# Revit family: Construction_Roof-Accessories_Alpine-SnowGuards_PD41
name_source: partatom
category: Specialty Equipment
units: mm (PartAtom-declared; Revit-internal decimal feet)

## family parameters
Cut with Voids When Loaded = No
Host = Face
OmniClass Number = 23.35.20.31.27.14
OmniClass Title = Snow Guards
Part Type = Normal
Room Calculation Point = No
Round Connector Dimension = Use Diameter
Shared = No

## types (5) — shared parameters
Assembly Code = B3010
Default Elevation = 48"
Description = PD41 Half Round Pad Style Snow Guard With Hook
Edition number = 1
Keynote = 07720
Manufacturer = Alpine SnowGuards
Model = PD 41
PD 410F = No
Product Guid = ab2724ba-9bd9-445f-86f5-17aeb9849d5a
Product Material = Alpine SnowGuards - Copper - Mill Finish
Product data url = https://www.bimobject.com
URL = https://www.alpinesnowguards.com
z_Option1 = Row Options : One Row
z_Option2 = Row Options : Two Rows
z_Option3 = Row Options : Three Rows

## per-type parameters (varying)
| type | Horizontal Spacing | Number of Rows | Vertical Spacing | Z_CR | Z_Horizontal Spacing | Z_Vertical Spacing |
| 3-Row Pattern | 24" | Row Options : Three Rows | 12" | No | 24" | 12" |
| 2x4 Pattern – Two Row | 48" | Row Options : Two Rows | 24" | No | 48" | 24" |
| 2x3 Pattern – Two Row | 36" | Row Options : Two Rows | 24" | No | 36" | 24" |
| 2x2 Pattern – Two Row | 24" | Row Options : Two Rows | 24" | No | 24" | 24" |
| Custom – Single Row | 24" | Row Options : One Row | 0" | Yes | 24" | 12" |

## geometry (parser evidence)
native form markers: Sweep x10
no freeform markers — native parametric forms only
